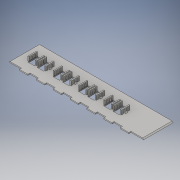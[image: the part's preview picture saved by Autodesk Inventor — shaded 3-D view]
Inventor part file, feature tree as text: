
AUTODESK INVENTOR PART (.ipt)
format: ipt  version: 2016 (Build 200138000, 138)  size: 399,872 bytes
history: native  units: in
note: dims shown in document units (in); Inventor stores cm internally (conversion verified against a paired STEP export)
features: extrude x5, sketch x5, chamfer x2, fillet x1
ambient origin geometry x8: Origin, YZ Plane, XZ Plane, XY Plane, X Axis, Y Axis, Z Axis, Center Point
bodies: Solid1 (feature_tree)
feature tree (13):
  extrude  "Extrusion1"  Depth=0.125in TaperAngle=0.0deg
  extrude  "Extrusion2"  Depth=0.125in TaperAngle=0.0deg
  extrude  "Extrusion4"  Depth=0.3937in
  extrude  "Extrusion5"  Depth=0.5in TaperAngle=0.0deg
  chamfer  "Chamfer1"  Distance=16.0in
  fillet  "Fillet1"  Radius=0.125in
  chamfer  "Chamfer2"  Distance=0.125in Angle=45.0deg
  sketch  "Sketch1"  dims[d0=16.0in d1=3.5in d2=0.125in d3=0.0in]
  sketch  "Sketch3"  dims[d5=2.7559in d7=0.3937in d8=2.0in d9=1.0in d10=0.125in d11=0.0in]
  sketch  "Sketch5"  dims[d22=1.5748in d24=3.0in d25=0.3937in d27=1.0in d29=0.5in d30=0.0in d31=16.0in d32=0.0in]
  sketch  "Sketch6"  dims[d33=0.125in d34=0.125in d35=45.0deg d36=0.125in d37=0.125in d38=0.125in d39=45.0deg]
  extrude  "Extrusion3"  [1 undecoded]
  sketch  "Sketch4"  dims[d12=1.0in d13=3.0in d15=0.3937in d17=1.5748in d19=0.0in d20=0.1969in d21=0.1969in]
note: 1 required parameter value undecoded (feature->parameter linkage not recoverable at this tier; creation-order binding heuristic only, values carry confidence <= 0.55)
